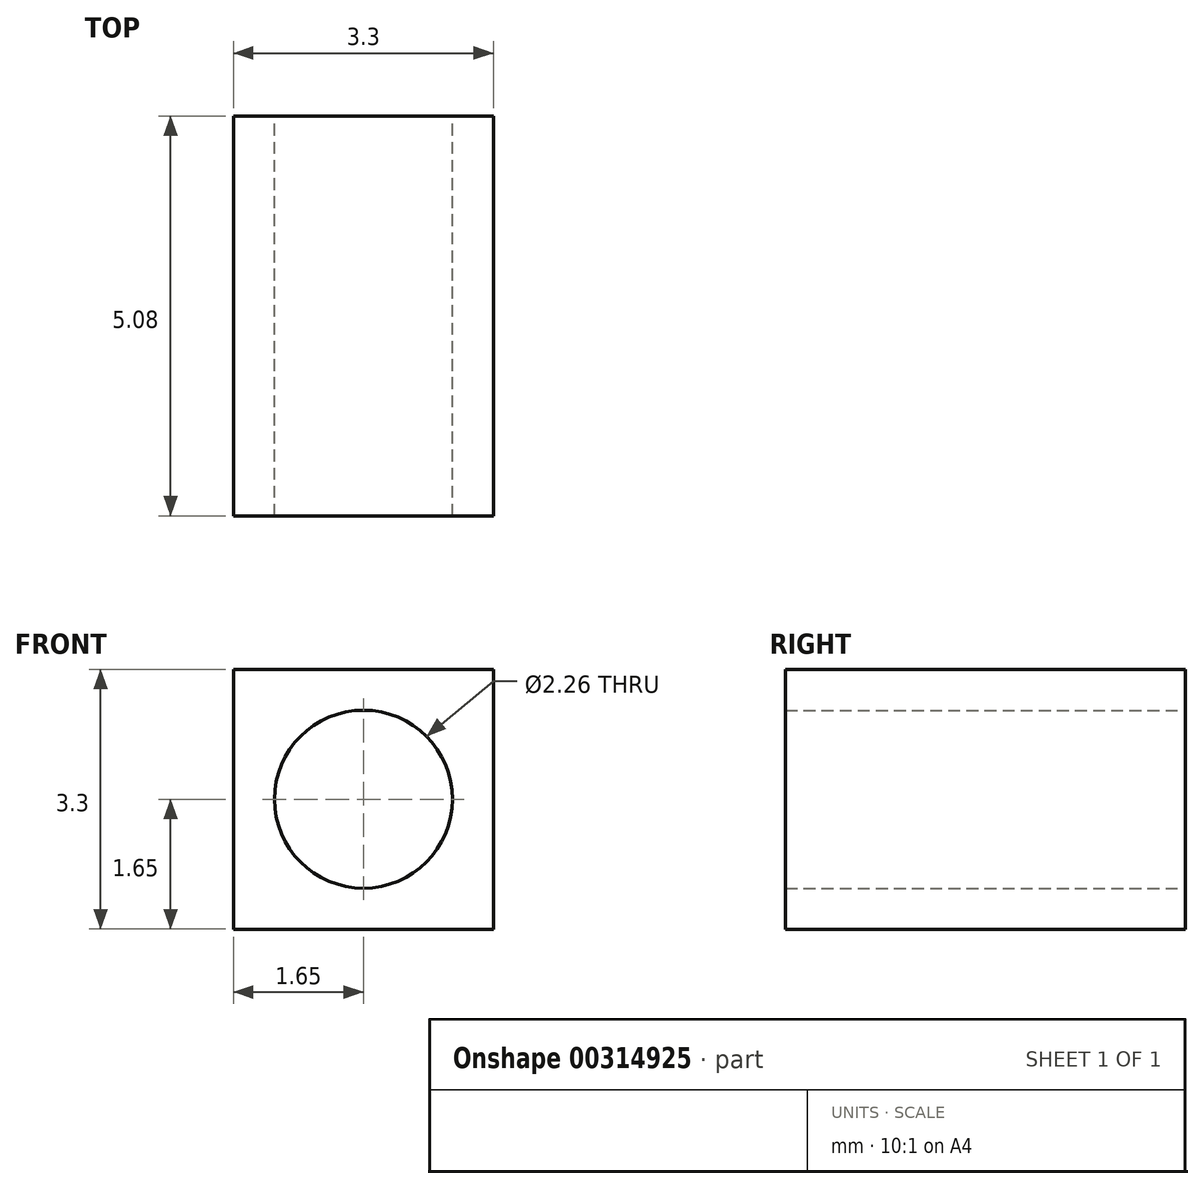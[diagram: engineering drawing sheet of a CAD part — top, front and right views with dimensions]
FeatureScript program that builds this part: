
annotation { "Feature Type Name" : "Feature", "Feature Type Description" : "" }
export const myFeature = defineFeature(function(context is Context, id is Id, definition is map)
    precondition{}
    {
        {
            var Q0;
            Q0=qCreatedBy(makeId("Front.planeOp"),FACE);
            var sketch = newSketch(context, id + "F0", { "sketchPlane" : qUnion([Q0])});
            skLineSegment(sketch, "E0.bottom", {"start": v(1.65, 1.65) * mm, "end": v(-1.65, 1.65) * mm});
            skLineSegment(sketch, "E0.top", {"start": v(1.65, -1.65) * mm, "end": v(-1.65, -1.65) * mm});
            skLineSegment(sketch, "E0.left", {"start": v(1.65, 1.65) * mm, "end": v(1.65, -1.65) * mm});
            skLineSegment(sketch, "E0.right", {"start": v(-1.65, 1.65) * mm, "end": v(-1.65, -1.65) * mm});
            skPoint(sketch, "E0.middle", {"position": v(0, 0) * mm});
            skCircle(sketch, "E1", {"center": v(0, 0) * mm, "radius": 1.13 * mm});
            skSolve(sketch);
        }
        {
            var Q0;
            Q0=makeQuery(id+"F0.imprint","IMPRINT",FACE,{"disambiguationData":[TD([[makeQuery(id+"F0.imprint","IMPRINT",EDGE,{"derivedFrom":sQuery(id+"F0.wireOp",EDGE,"E0.bottom")}),1.0]])]});
            extrude(context, id + "F1", {"entities" : qUnion([Q0]), "depth" : 5.08 * mm});
        }
    });
